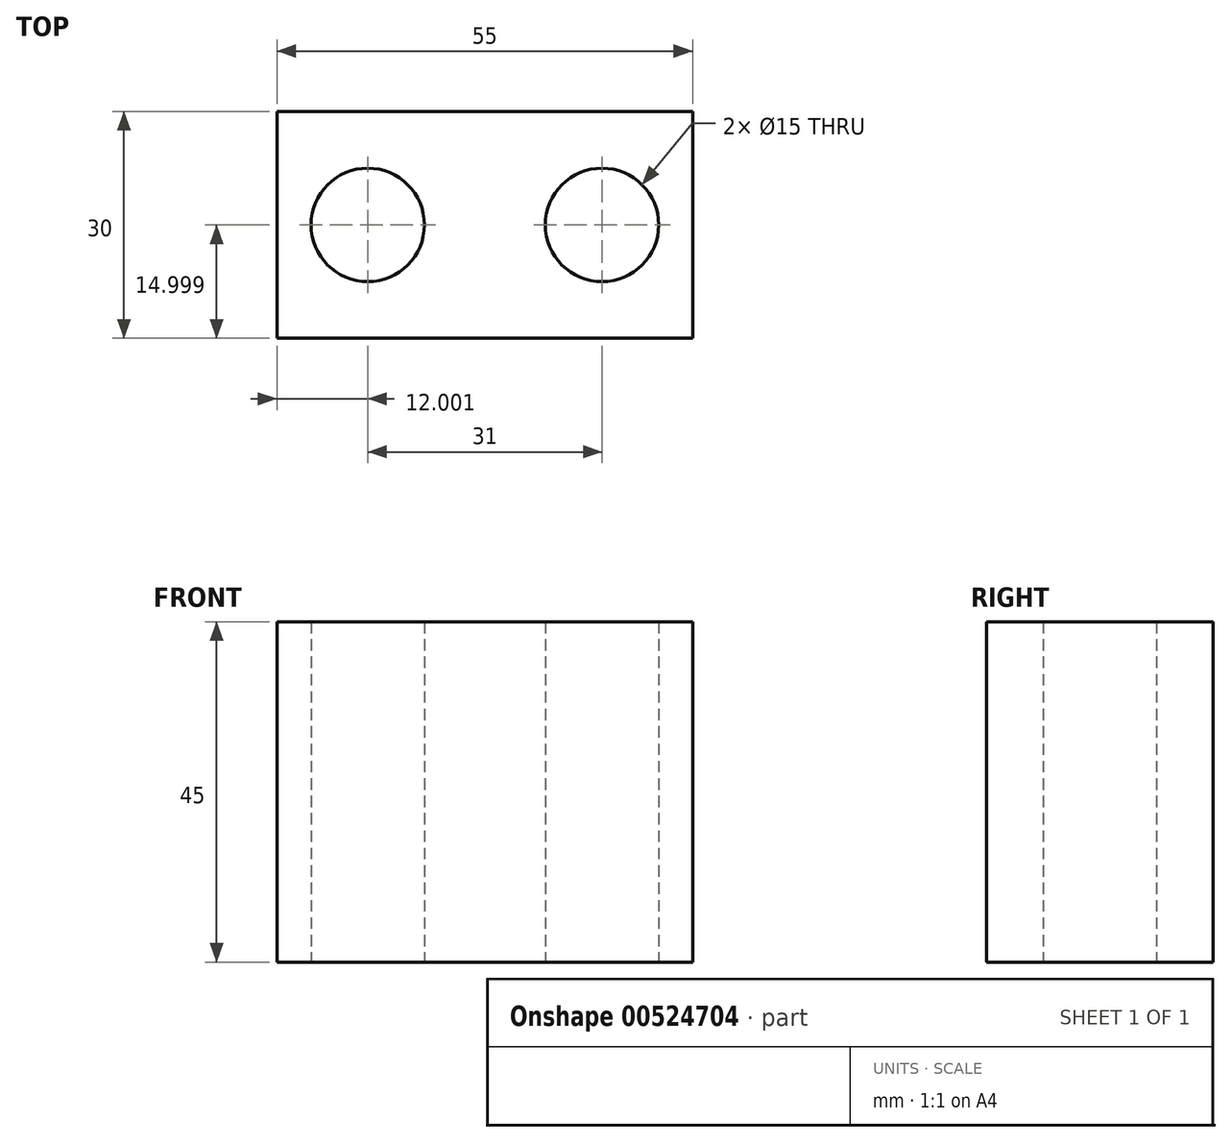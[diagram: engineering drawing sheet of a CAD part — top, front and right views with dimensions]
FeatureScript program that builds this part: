
annotation { "Feature Type Name" : "Feature", "Feature Type Description" : "" }
export const myFeature = defineFeature(function(context is Context, id is Id, definition is map)
    precondition{}
    {
        {
            var Q0;
            Q0=qCreatedBy(makeId("Top.planeOp"),FACE);
            var sketch = newSketch(context, id + "F0", { "sketchPlane" : qUnion([Q0])});
            skCircle(sketch, "E0", {"center": v(-40.84, 32.54) * mm, "radius": 7.5 * mm});
            skCircle(sketch, "E1", {"center": v(-9.84, 32.54) * mm, "radius": 7.5 * mm});
            skLineSegment(sketch, "E2.bottom", {"start": v(-52.84, 47.54) * mm, "end": v(2.16, 47.54) * mm});
            skLineSegment(sketch, "E2.top", {"start": v(-52.84, 17.54) * mm, "end": v(2.16, 17.54) * mm});
            skLineSegment(sketch, "E2.left", {"start": v(-52.84, 47.54) * mm, "end": v(-52.84, 17.54) * mm});
            skLineSegment(sketch, "E2.right", {"start": v(2.16, 47.54) * mm, "end": v(2.16, 17.54) * mm});
            skSolve(sketch);
        }
        {
            var Q0;
            Q0=makeQuery(id+"F0.imprint","IMPRINT",FACE,{"disambiguationData":[TD([[makeQuery(id+"F0.imprint","IMPRINT",EDGE,{"derivedFrom":sQuery(id+"F0.wireOp",EDGE,"E0")}),-1.0]])]});
            extrude(context, id + "F1", {"entities" : qUnion([Q0]), "depth" : 45 * mm, "offsetDistance" : 25 * mm});
        }
    });
